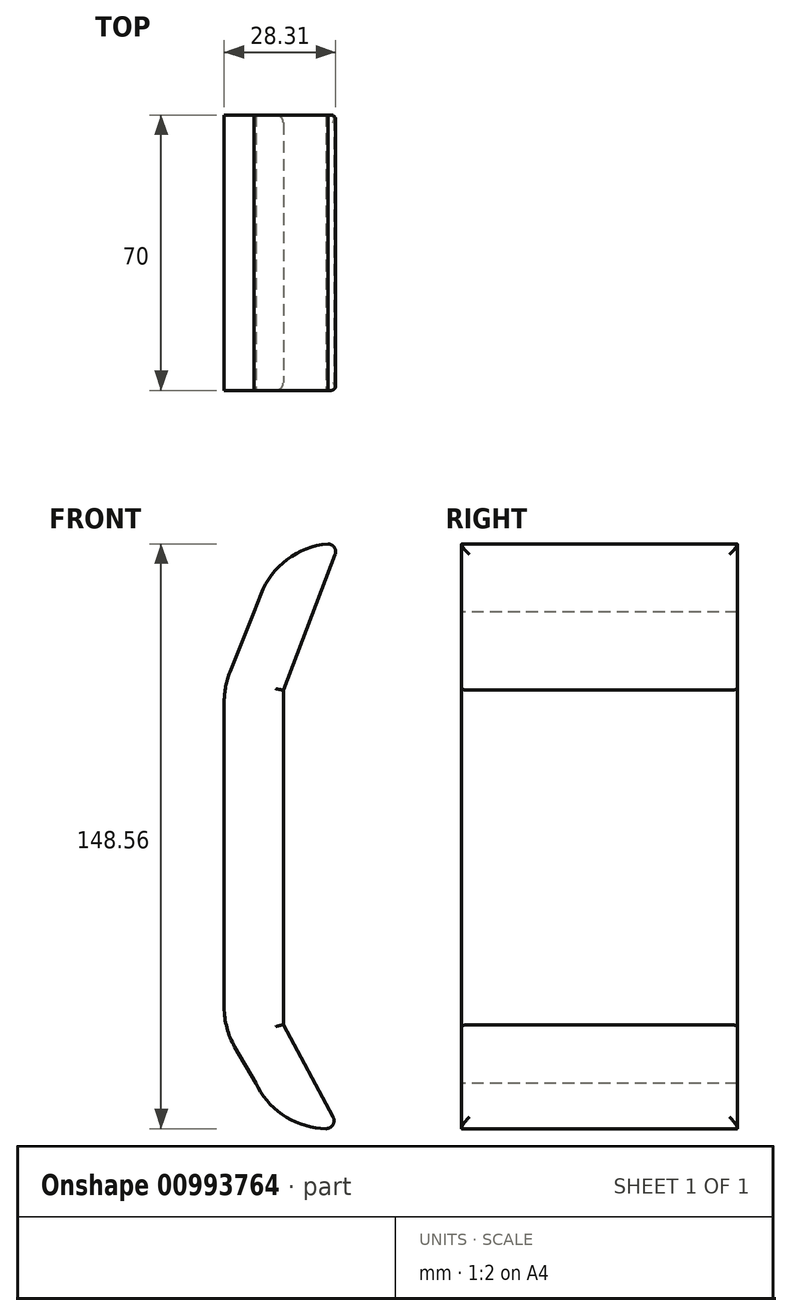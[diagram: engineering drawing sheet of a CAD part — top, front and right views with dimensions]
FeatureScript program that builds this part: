
annotation { "Feature Type Name" : "Feature", "Feature Type Description" : "" }
export const myFeature = defineFeature(function(context is Context, id is Id, definition is map)
    precondition{}
    {
        {
            var Q0;
            Q0=qCreatedBy(makeId("Right.planeOp"),FACE);
            var sketch = newSketch(context, id + "F0", { "sketchPlane" : qUnion([Q0])});
            skLineSegment(sketch, "E0.bottom", {"start": v(-35, 60) * mm, "end": v(35, 60) * mm});
            skLineSegment(sketch, "E0.top", {"start": v(-35, -60) * mm, "end": v(35, -60) * mm});
            skLineSegment(sketch, "E0.left", {"start": v(-35, 60) * mm, "end": v(-35, -60) * mm});
            skLineSegment(sketch, "E0.right", {"start": v(35, 60) * mm, "end": v(35, -60) * mm});
            skPoint(sketch, "E0.middle", {"position": v(0, 0) * mm});
            skSolve(sketch);
        }
        {
            var Q0;
            Q0=makeQuery(id+"F0.imprint","IMPRINT",FACE,{"disambiguationData":[TD([[makeQuery(id+"F0.imprint","IMPRINT",EDGE,{"derivedFrom":sQuery(id+"F0.wireOp",EDGE,"E0.bottom")}),-1.0]])]});
            extrude(context, id + "F1", {"entities" : qUnion([Q0]), "endBound" : BoundingType.SYMMETRIC, "depth" : 15 * mm, "offsetDistance" : 25 * mm});
        }
        {
            var Q0;
            Q0=makeQuery(id+"F1.opExtrude","SWEPT_FACE",FACE,{"disambiguationData":[OSD([sQuery(id+"F0.wireOp",EDGE,"E0.left")])]});
            var sketch = newSketch(context, id + "F2", { "sketchPlane" : qUnion([Q0])});
            skLineSegment(sketch, "E1", {"start": v(-7.5, 0) * mm, "end": v(-7.5, 40) * mm});
            skLineSegment(sketch, "E2", {"start": v(-7.5, 40) * mm, "end": v(6.72, 77.14) * mm});
            skLineSegment(sketch, "E3", {"start": v(6.72, 77.14) * mm, "end": v(21.72, 77.14) * mm});
            skLineSegment(sketch, "E4", {"start": v(21.72, 77.14) * mm, "end": v(7.5, 40) * mm});
            skLineSegment(sketch, "E5", {"start": v(7.5, 40) * mm, "end": v(-7.5, 40) * mm});
            skLineSegment(sketch, "E6", {"start": v(-7.5, 0) * mm, "end": v(-7.5, -45) * mm});
            skLineSegment(sketch, "E7", {"start": v(-7.5, -45) * mm, "end": v(6.72, -71.42) * mm});
            skLineSegment(sketch, "E8", {"start": v(6.72, -71.42) * mm, "end": v(21.72, -71.42) * mm});
            skLineSegment(sketch, "E9", {"start": v(21.72, -71.42) * mm, "end": v(7.5, -45) * mm});
            skLineSegment(sketch, "E10", {"start": v(7.5, -45) * mm, "end": v(-7.5, -45) * mm});
            skSolve(sketch);
        }
        {
            var Q0;
            Q0 = qSketchRegion(id + "F2", true);
            var Q1;
            Q1=makeQuery(id+"F1.opExtrude","SWEPT_BODY",BODY,{"disambiguationData":[OSD([sQuery(id+"F0.wireOp",EDGE,"E0.bottom"),sQuery(id+"F0.wireOp",EDGE,"E0.top"),sQuery(id+"F0.wireOp",EDGE,"E0.left"),sQuery(id+"F0.wireOp",EDGE,"E0.right")])]});
            extrude(context, id + "F3", {"entities" : qUnion([Q0]), "operationType" : NewBodyOperationType.ADD, "oppositeDirection" : true, "depth" : 70 * mm, "endBoundEntityBody" : qUnion([Q1]), "offsetDistance" : 25 * mm});
        }
        {
            var Q0;
            Q0=makeQuery(id+"F1.opExtrude","CAP_EDGE",EDGE,{"disambiguationData":[OSD([sQuery(id+"F0.wireOp",EDGE,"E0.bottom")])],"isStart":true});
            chamfer(context, id + "F4", {"entities" : qUnion([Q0]), "chamferType" : ChamferType.TWO_OFFSETS, "width1" : 19 * mm, "oppositeDirection" : false, "width2" : 7.66 * mm, "tangentPropagation" : true});
        }
        {
            var Q0;
            Q0=makeQuery(id+"F1.opExtrude","CAP_EDGE",EDGE,{"disambiguationData":[OSD([sQuery(id+"F0.wireOp",EDGE,"E0.top")])],"isStart":true});
            chamfer(context, id + "F5", {"entities" : qUnion([Q0]), "chamferType" : ChamferType.TWO_OFFSETS, "width1" : 8.08 * mm, "oppositeDirection" : false, "width2" : 14 * mm, "tangentPropagation" : true});
        }
        {
            var Q0;
            Q0=makeQuery(id+"F3.opExtrude","CAP_EDGE",EDGE,{"disambiguationData":[OSD([sQuery(id+"F2.wireOp",EDGE,"E4")])],"isStart":true});
            var Q1;
            Q1=makeQuery(id+"F1.opExtrude","CAP_EDGE",EDGE,{"disambiguationData":[OSD([sQuery(id+"F0.wireOp",EDGE,"E0.left")])],"isStart":false});
            var Q2;
            Q2=makeQuery(id+"F3.opExtrude","CAP_EDGE",EDGE,{"disambiguationData":[OSD([sQuery(id+"F2.wireOp",EDGE,"E9")])],"isStart":true});
            var Q3;
            Q3=makeQuery(id+"F3.opExtrude","CAP_EDGE",EDGE,{"disambiguationData":[OSD([sQuery(id+"F2.wireOp",EDGE,"E9")])],"isStart":false});
            var Q4;
            Q4=makeQuery(id+"F1.opExtrude","CAP_EDGE",EDGE,{"disambiguationData":[OSD([sQuery(id+"F0.wireOp",EDGE,"E0.right")])],"isStart":false});
            var Q5;
            Q5=makeQuery(id+"F3.opExtrude","CAP_EDGE",EDGE,{"disambiguationData":[OSD([sQuery(id+"F2.wireOp",EDGE,"E4")])],"isStart":false});
            var Q6;
            Q6=makeQuery(id+"F3.opExtrude","SWEPT_EDGE",EDGE,{"disambiguationData":[OSD([sQuery(id+"F2.wireOp",EDGE,"E3"),sQuery(id+"F2.wireOp",EDGE,"E4")])]});
            var Q7;
            Q7=makeQuery(id+"F3.opExtrude","SWEPT_EDGE",EDGE,{"disambiguationData":[OSD([sQuery(id+"F2.wireOp",EDGE,"E8"),sQuery(id+"F2.wireOp",EDGE,"E9")])]});
            fillet(context, id + "F6", {"entities" : qUnion([Q0, Q1, Q2, Q3, Q4, Q5, Q6, Q7]), "radius" : 2 * mm, "tangentPropagation" : true, "allowEdgeOverflow" : false});
        }
        {
            var Q0;
            {var subQ0=sQuery(id+"F0.wireOp",EDGE,"E0.bottom");Q0=makeQuery(id+"F4.opChamfer","BLEND_EDGE",EDGE,{"blendedFrom":[makeQuery(id+"F1.opExtrude","CAP_EDGE",EDGE,{"disambiguationData":[OSD([subQ0])],"isStart":true}),makeQuery(id+"F1.opExtrude","CAP_FACE",FACE,{"disambiguationData":[OSD([subQ0,sQuery(id+"F0.wireOp",EDGE,"E0.top"),sQuery(id+"F0.wireOp",EDGE,"E0.left"),sQuery(id+"F0.wireOp",EDGE,"E0.right")])],"isStart":true})],"blendedInto":[makeQuery(id+"F1.opExtrude","CAP_FACE",FACE,{"disambiguationData":[OSD([subQ0,sQuery(id+"F0.wireOp",EDGE,"E0.top"),sQuery(id+"F0.wireOp",EDGE,"E0.left"),sQuery(id+"F0.wireOp",EDGE,"E0.right")])],"isStart":true})]});}
            var Q1;
            {var subQ0=sQuery(id+"F0.wireOp",EDGE,"E0.top");Q1=makeQuery(id+"F5.opChamfer","BLEND_EDGE",EDGE,{"blendedFrom":[makeQuery(id+"F1.opExtrude","CAP_EDGE",EDGE,{"disambiguationData":[OSD([subQ0])],"isStart":true}),makeQuery(id+"F1.opExtrude","CAP_FACE",FACE,{"disambiguationData":[OSD([sQuery(id+"F0.wireOp",EDGE,"E0.bottom"),subQ0,sQuery(id+"F0.wireOp",EDGE,"E0.left"),sQuery(id+"F0.wireOp",EDGE,"E0.right")])],"isStart":true})],"blendedInto":[makeQuery(id+"F1.opExtrude","CAP_FACE",FACE,{"disambiguationData":[OSD([sQuery(id+"F0.wireOp",EDGE,"E0.bottom"),subQ0,sQuery(id+"F0.wireOp",EDGE,"E0.left"),sQuery(id+"F0.wireOp",EDGE,"E0.right")])],"isStart":true})]});}
            var Q2;
            Q2=makeQuery(id+"F3.opExtrude","SWEPT_EDGE",EDGE,{"disambiguationData":[OSD([sQuery(id+"F2.wireOp",EDGE,"E2"),sQuery(id+"F2.wireOp",EDGE,"E3")])]});
            var Q3;
            Q3=makeQuery(id+"F3.opExtrude","SWEPT_EDGE",EDGE,{"disambiguationData":[OSD([sQuery(id+"F2.wireOp",EDGE,"E7"),sQuery(id+"F2.wireOp",EDGE,"E8")])]});
            fillet(context, id + "F7", {"entities" : qUnion([Q0, Q1, Q2, Q3]), "radius" : 20 * mm, "tangentPropagation" : true, "allowEdgeOverflow" : false});
        }
    });
